annotation { "Feature Type Name" : "Feature", "Feature Type Description" : "" }
export const myFeature = defineFeature(function(context is Context, id is Id, definition is map)
    precondition{}
    {
        {
            var Q0;
            Q0=qCreatedBy(makeId("Front.planeOp"),FACE);
            var sketch = newSketch(context, id + "F0", { "sketchPlane" : qUnion([Q0])});
            skLineSegment(sketch, "E0.top", {"start": v(-40.18, 0.1) * mm, "end": v(39.63, 0.1) * mm});
            skLineSegment(sketch, "E0.left", {"start": v(-40.18, 40) * mm, "end": v(-40.18, 0.1) * mm});
            skLineSegment(sketch, "E0.right", {"start": v(39.63, 40) * mm, "end": v(39.63, 0.1) * mm});
            skPoint(sketch, "E1", {"position": v(0, 40) * mm});
            skPoint(sketch, "E2", {"position": v(-0.27, 40) * mm});
            skPoint(sketch, "E3", {"position": v(-16.23, 40) * mm});
            skPoint(sketch, "E4", {"position": v(15.7, 40) * mm});
            skArc(sketch, "E5", {"start": v(15.7, 40) * mm, "mid": v(-0.27, 56.3) * mm, "end": v(-16.23, 40) * mm});
            skLineSegment(sketch, "E6", {"start": v(-40.18, 40) * mm, "end": v(-16.23, 40) * mm});
            skLineSegment(sketch, "E7", {"start": v(15.7, 40) * mm, "end": v(39.63, 40) * mm});
            skLineSegment(sketch, "E8", {"start": v(-16.23, 40) * mm, "end": v(-40.18, 40) * mm});
            skPoint(sketch, "E9", {"position": v(0, 40.64) * mm});
            skCircle(sketch, "E10", {"center": v(0, 40.64) * mm, "radius": 2.5 * mm});
            skText(sketch, "E11", { "text": "John Hitler", "fontName": "Tinos-Regular.ttf"});
            const initialGuessF0  = {"E11": [-0.03, 0.0259, 1, 0, 0.00955]};
            skSetInitialGuess(sketch, initialGuessF0);
            skSolve(sketch);
        }
        {
            var Q0;
            Q0 = qSketchRegion(id + "F0", true);
            extrude(context, id + "F1", {"entities" : qUnion([Q0]), "depth" : 10 * mm});
        }
    });